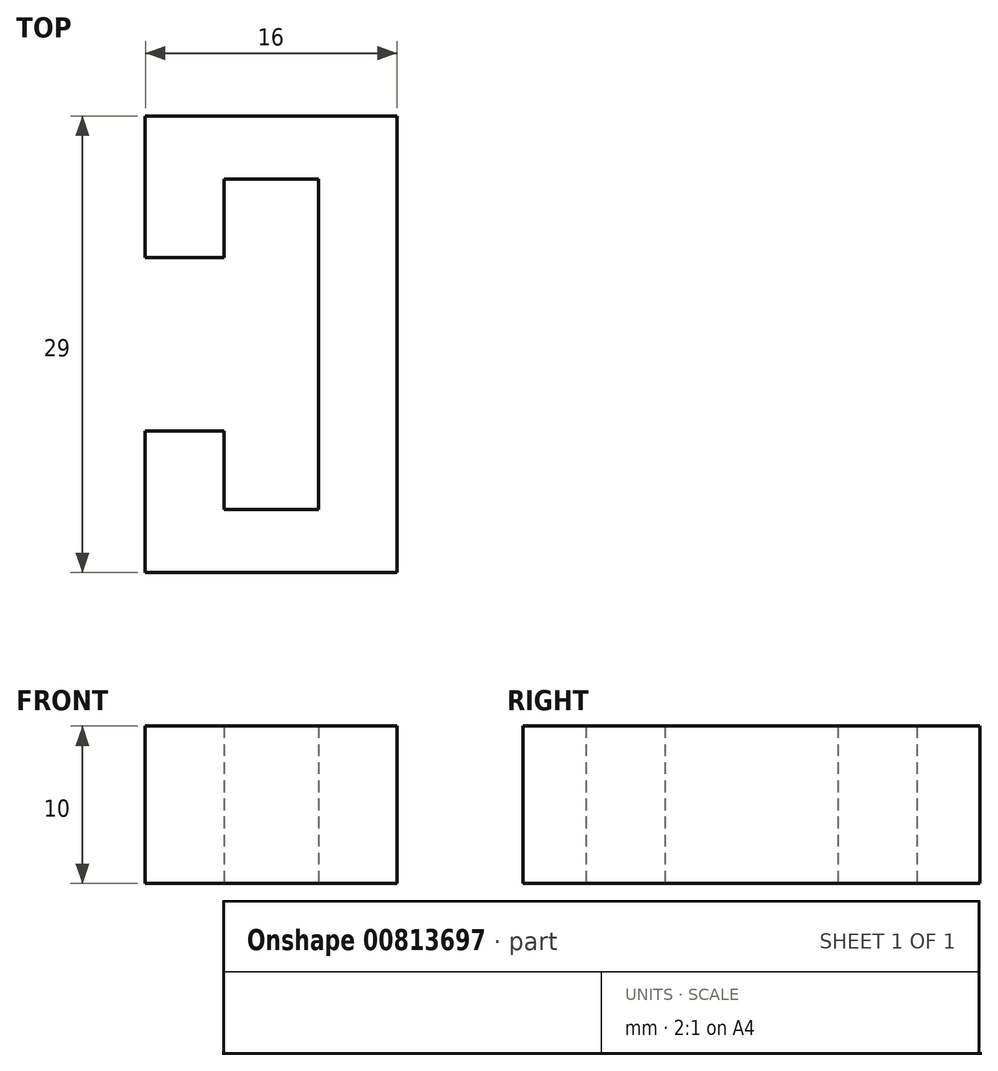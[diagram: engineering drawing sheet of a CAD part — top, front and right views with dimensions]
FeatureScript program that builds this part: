
annotation { "Feature Type Name" : "Feature", "Feature Type Description" : "" }
export const myFeature = defineFeature(function(context is Context, id is Id, definition is map)
    precondition{}
    {
        {
            var Q0;
            Q0=qCreatedBy(makeId("Top.planeOp"),FACE);
            var sketch = newSketch(context, id + "F0", { "sketchPlane" : qUnion([Q0])});
            skLineSegment(sketch, "E0.0", {"start": v(-26, 12.03) * mm, "end": v(-21, 12.03) * mm});
            skLineSegment(sketch, "E0.1", {"start": v(-21, 12.03) * mm, "end": v(-21, 17.03) * mm});
            skLineSegment(sketch, "E0.2", {"start": v(-15, 17.03) * mm, "end": v(-21, 17.03) * mm});
            skLineSegment(sketch, "E0.3", {"start": v(-15, -3.97) * mm, "end": v(-15, 17.03) * mm});
            skLineSegment(sketch, "E0.4", {"start": v(-15, -3.97) * mm, "end": v(-21, -3.97) * mm});
            skLineSegment(sketch, "E0.5", {"start": v(-21, -3.97) * mm, "end": v(-21, 1.03) * mm});
            skLineSegment(sketch, "E0.6", {"start": v(-26, 1.03) * mm, "end": v(-21, 1.03) * mm});
            skLineSegment(sketch, "E1", {"start": v(-26, 1.03) * mm, "end": v(-26, -7.97) * mm});
            skLineSegment(sketch, "E2", {"start": v(-26, -7.97) * mm, "end": v(-10, -7.97) * mm});
            skLineSegment(sketch, "E3", {"start": v(-10, -7.97) * mm, "end": v(-10, 21.03) * mm});
            skLineSegment(sketch, "E4", {"start": v(-10, 21.03) * mm, "end": v(-26, 21.03) * mm});
            skLineSegment(sketch, "E5", {"start": v(-26, 21.03) * mm, "end": v(-26, 12.03) * mm});
            skSolve(sketch);
        }
        {
            var Q0;
            Q0 = qSketchRegion(id + "F0", true);
            extrude(context, id + "F1", {"entities" : qUnion([Q0]), "depth" : 10 * mm, "offsetDistance" : 25 * mm});
        }
    });
